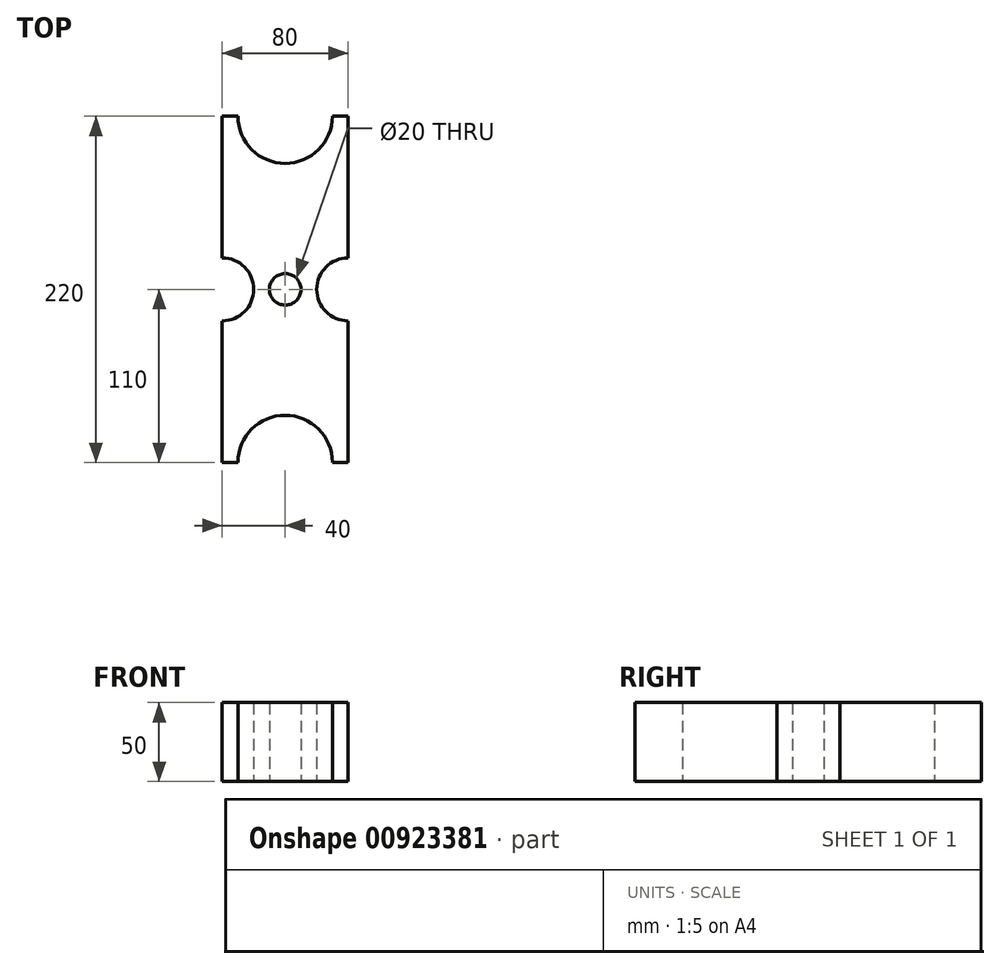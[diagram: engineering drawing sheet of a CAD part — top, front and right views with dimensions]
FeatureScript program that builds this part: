
annotation { "Feature Type Name" : "Feature", "Feature Type Description" : "" }
export const myFeature = defineFeature(function(context is Context, id is Id, definition is map)
    precondition{}
    {
        {
            var Q0;
            Q0=qCreatedBy(makeId("Top.planeOp"),FACE);
            var sketch = newSketch(context, id + "F0", { "sketchPlane" : qUnion([Q0])});
            skLineSegment(sketch, "E0.bottom", {"start": v(40, -110) * mm, "end": v(30, -110) * mm});
            skLineSegment(sketch, "E0.top", {"start": v(40, 110) * mm, "end": v(30, 110) * mm});
            skLineSegment(sketch, "E0.left", {"start": v(40, -110) * mm, "end": v(40, -20) * mm});
            skLineSegment(sketch, "E0.right", {"start": v(-40, -110) * mm, "end": v(-40, -20) * mm});
            skPoint(sketch, "E0.middle", {"position": v(0, 0) * mm});
            skLineSegment(sketch, "E1", {"start": v(-40, 110) * mm, "end": v(-40, 20) * mm});
            skLineSegment(sketch, "E2", {"start": v(40, 110) * mm, "end": v(40, 20) * mm});
            skLineSegment(sketch, "E3", {"start": v(-40, 20) * mm, "end": v(40, 20) * mm});
            skLineSegment(sketch, "E4", {"start": v(-40, -20) * mm, "end": v(40, -20) * mm});
            skCircle(sketch, "E5", {"center": v(0, 0) * mm, "radius": 10 * mm});
            skLineSegment(sketch, "E6", {"start": v(-40, -110) * mm, "end": v(-30, -110) * mm});
            skLineSegment(sketch, "E7", {"start": v(-40, 110) * mm, "end": v(-30, 110) * mm});
            skArc(sketch, "E8", {"start": v(-30, 110) * mm, "mid": v(0, 80) * mm, "end": v(30, 110) * mm});
            skLineSegment(sketch, "E9.trimOffspring", {"start": v(-30, 110) * mm, "end": v(-40, 110) * mm});
            skArc(sketch, "E10", {"start": v(30, -110) * mm, "mid": v(0, -80) * mm, "end": v(-30, -110) * mm});
            skLineSegment(sketch, "E11.trimOffspring", {"start": v(-30, -110) * mm, "end": v(-40, -110) * mm});
            skArc(sketch, "E12", {"start": v(-40, -20) * mm, "mid": v(-20, 0) * mm, "end": v(-40, 20) * mm});
            skLineSegment(sketch, "E13.trimOffspring", {"start": v(-40, 20) * mm, "end": v(-40, 110) * mm});
            skArc(sketch, "E14", {"start": v(40, 20) * mm, "mid": v(20, 0) * mm, "end": v(40, -20) * mm});
            skLineSegment(sketch, "E15.trimOffspring", {"start": v(40, 20) * mm, "end": v(40, 110) * mm});
            skSolve(sketch);
        }
        {
            var Q0;
            Q0=makeQuery(id+"F0.imprint","IMPRINT",FACE,{"disambiguationData":[TD([[makeQuery(id+"F0.imprint","IMPRINT",EDGE,{"derivedFrom":sQuery(id+"F0.wireOp",EDGE,"E3")}),1.0]])]});
            var Q1;
            Q1=makeQuery(id+"F0.imprint","IMPRINT",FACE,{"disambiguationData":[TD([[makeQuery(id+"F0.imprint","IMPRINT",EDGE,{"derivedFrom":sQuery(id+"F0.wireOp",EDGE,"E0.right")}),-1.0]])]});
            var Q2;
            Q2=makeQuery(id+"F0.imprint","IMPRINT",FACE,{"disambiguationData":[TD([[makeQuery(id+"F0.imprint","IMPRINT",EDGE,{"derivedFrom":sQuery(id+"F0.wireOp",EDGE,"E3")}),-1.0]])]});
            extrude(context, id + "F1", {"entities" : qUnion([Q0, Q1, Q2]), "depth" : 25 * mm, "offsetDistance" : 25 * mm, "hasSecondDirection" : true, "secondDirectionOppositeDirection" : true, "secondDirectionDepth" : 25 * mm});
        }
    });
